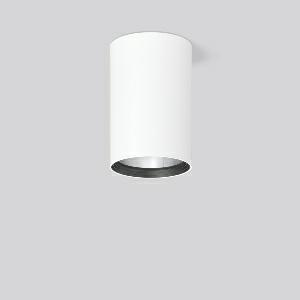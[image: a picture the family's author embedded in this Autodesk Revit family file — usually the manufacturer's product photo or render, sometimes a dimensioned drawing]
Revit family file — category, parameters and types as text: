
# Revit family: heledon_maxi_a_931225_002_8f8f
name_source: partatom
category: Lighting Fixtures
units: mm (PartAtom-declared; Revit-internal decimal feet)

## family parameters
Cut with Voids When Loaded = No
Host = Face
Light Source = No
Part Type = Normal
Room Calculation Point = No
Round Connector Dimension = Use Diameter
Shared = No

## types (1)
- HELEDON maxi A (1 x LED Modul 930, 4350 lm, 3000)
    Apparent Load = 35 VA
    Approval mark = CE
    CIE Flux Codes = 100 100 100 100 100
    Color Rendering = 90
    Color Temperature = 3000
    Default Elevation = 1800 mm
    Description = Series: HELEDON maxi
Cylindrical surface-mounted downlight. Housing: die-cast aluminium, powder-coated. Internal ceiling frame polycarbonate with bayonet mounting. Black plastic ring and recessed LED to prevent glare from the side. Optical assembly with reflector made of MIRO-Silver with 98% total light reflection for outstanding efficiency - can be changed without tools. Best colour rendering index Ra>90. Suitable for Ceiling mounting. Easy installation with a separate ceiling frame with bayonet mounting and plug connection. Driver integrated. Connected via plug-in connector. High quality converter without flickering and stroboscopic effect. The following accessories can be mounted without use of tools: interchangeable lenses, decorative glasses, honeycomb louvre, clear and frosted diffusers, white interchangeable plastic ring. 
Colour: traffic white, matt (RAL 9016)
Diameter: 123 mm
Height: 183 mm
Lamp: LED
Socket: without socket
Colour temperature: 3000K
Colour rendering index (CRI): 92
System power: 35 W
Rated luminous flux: 4350 lm
Luminous efficiency: 124 lm/W
Control gear: Regulated power supply
Protection class: I
Type of protection: IP 20
    Height = 183 mm
    Lamp = 1 x LED Modul 930
    Lamp Light Flux = 4350 lm
    Lamp count = 1
    Length = 123 mm
    Lifetime = 50000 h
    Luminous efficacy = 124 lm/W
    Manufacturer = RZB
    ModVariant = No
    Model = 931225.002
    Mounting Place = Ceiling
    Mounting Type = Surface mounted
    Number of Poles = 1
    OnlyDefault = Yes
    Power Factor = 1
    Product Name = HELEDON maxi A
    Product group = Surface mounted downlights
    ProductGroupID = 302
    Protection Class = Protection class I
    Protection Degree = IP 20
    RLX_Detail_Level = 1
    RLX_Emergency_Light_Flux = 0 lm
    RLX_Emergency_Type = 0
    RLX_Emergency_Type_DB = No
    RlxData = <blob elided: 95597 chars, md5=946ed186>
    Socket = socket
    Standby Power = 0 W
    System Light Flux = 4350 lm
    System Power = 35 W
    Type Comments = Product without accessories
    Type Image = 931192.002.jpg
    URL = http://relux.com
    VarID = ---
    Voltage = 230 V
    Voltage Range = 220-240 V
    Weight = 0.00 kg
    Width = 0 mm  [stored 0 ft]

note: [stored X ft] marks values corroborated as IEEE doubles in the binary element streams (Revit-internal decimal feet)

## geometry (parser evidence)
native form markers: Blend x4, Sweep x8
no freeform markers — native parametric forms only
